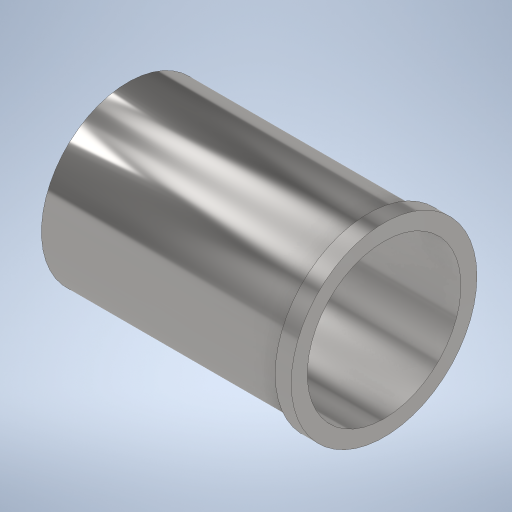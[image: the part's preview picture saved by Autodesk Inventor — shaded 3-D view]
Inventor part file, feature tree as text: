
AUTODESK INVENTOR PART (.ipt)
format: ipt  version: 2024 (Build 280153000, 153)  size: 280,576 bytes
history: native  units: mm
features: sketch x2, revolve x1, hole x1
ambient origin geometry x8: Origin, YZ Plane, XZ Plane, XY Plane, X Axis, Y Axis, Z Axis, Center Point
bodies: Volumenkörper1 (feature_tree)
feature tree (4):
  revolve  "Umdrehung1"
  hole  "Bohrung1"  [1 undecoded]
  sketch  "Skizze1"  dims[d0=29.0mm d1=27.0mm]
  sketch  "Skizze2"  dims[d2=2.5mm d3=37.5mm d4=90.0deg d5=24.0mm d6=6.0mm d7=4.0mm d8=2.0mm d9=90.0deg d10=8.0mm d11=20.594885mm]
note: 1 required parameter value undecoded (feature->parameter linkage not recoverable at this tier; creation-order binding heuristic only, values carry confidence <= 0.55)
